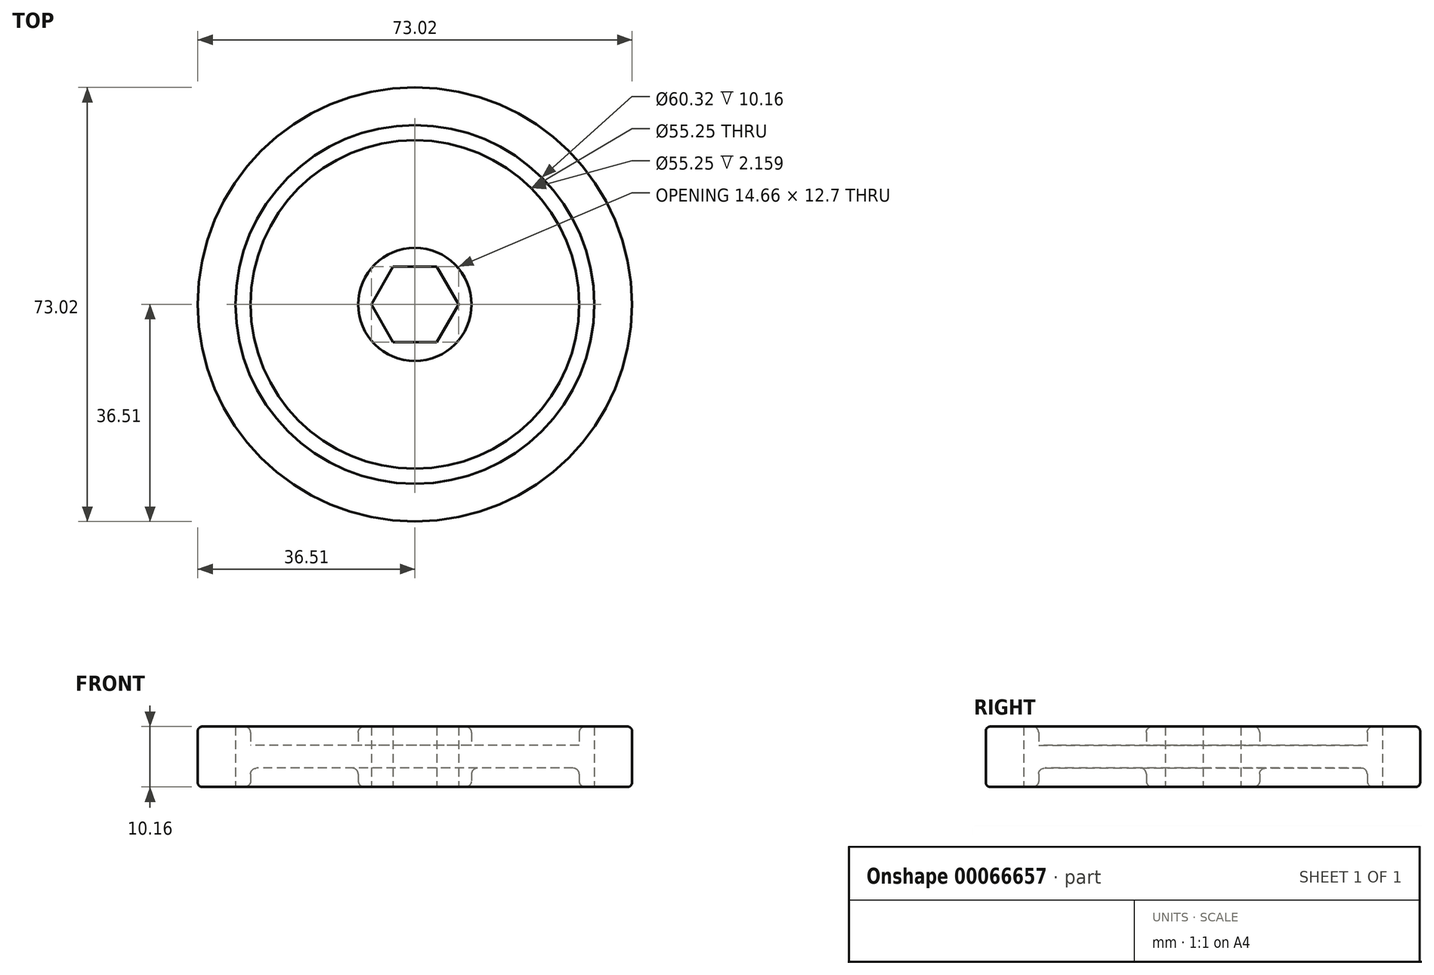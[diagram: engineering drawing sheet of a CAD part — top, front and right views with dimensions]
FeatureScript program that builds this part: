
annotation { "Feature Type Name" : "Feature", "Feature Type Description" : "" }
export const myFeature = defineFeature(function(context is Context, id is Id, definition is map)
    precondition{}
    {
        {
            var Q0;
            Q0=qCreatedBy(makeId("Top.planeOp"),FACE);
            var sketch = newSketch(context, id + "F0", { "sketchPlane" : qUnion([Q0])});
            skCircle(sketch, "E0", {"center": v(0, 0) * mm, "radius": 36.51 * mm});
            skCircle(sketch, "E1", {"center": v(0, 0) * mm, "radius": 27.62 * mm});
            skCircle(sketch, "E2", {"center": v(0, 0) * mm, "radius": 30.16 * mm});
            skCircle(sketch, "E3", {"center": v(0, 0) * mm, "radius": 9.53 * mm});
            skCircle(sketch, "E4.cCircle", {"center": v(0, 0) * mm, "radius": 6.35 * mm, "construction": true});
            skLineSegment(sketch, "E4.0", {"start": v(3.67, -6.35) * mm, "end": v(-3.67, -6.35) * mm});
            skLineSegment(sketch, "E4.1", {"start": v(-3.67, -6.35) * mm, "end": v(-7.33, 0) * mm});
            skLineSegment(sketch, "E4.2", {"start": v(-7.33, 0) * mm, "end": v(-3.67, 6.35) * mm});
            skLineSegment(sketch, "E4.3", {"start": v(-3.67, 6.35) * mm, "end": v(3.67, 6.35) * mm});
            skLineSegment(sketch, "E4.4", {"start": v(3.67, 6.35) * mm, "end": v(7.33, 0) * mm});
            skLineSegment(sketch, "E4.5", {"start": v(7.33, 0) * mm, "end": v(3.67, -6.35) * mm});
            skPoint(sketch, "E4.0.midPoint", {"position": v(0, -6.35) * mm});
            skSolve(sketch);
        }
        {
            var Q0;
            Q0=makeQuery(id+"F0.imprint","IMPRINT",FACE,{"disambiguationData":[TD([[makeQuery(id+"F0.imprint","IMPRINT",EDGE,{"derivedFrom":sQuery(id+"F0.wireOp",EDGE,"E1")}),-1.0]])]});
            var Q1;
            Q1=makeQuery(id+"F0.imprint","IMPRINT",FACE,{"disambiguationData":[TD([[makeQuery(id+"F0.imprint","IMPRINT",EDGE,{"derivedFrom":sQuery(id+"F0.wireOp",EDGE,"E3")}),1.0]])]});
            extrude(context, id + "F1", {"entities" : qUnion([Q0, Q1]), "endBound" : BoundingType.SYMMETRIC, "depth" : 10.16 * mm});
        }
        {
            var Q0;
            Q0=makeQuery(id+"F0.imprint","IMPRINT",FACE,{"disambiguationData":[TD([[makeQuery(id+"F0.imprint","IMPRINT",EDGE,{"derivedFrom":sQuery(id+"F0.wireOp",EDGE,"E1")}),1.0]])]});
            extrude(context, id + "F2", {"entities" : qUnion([Q0]), "operationType" : NewBodyOperationType.ADD, "endBound" : BoundingType.SYMMETRIC, "depth" : 3.8 * mm});
        }
        {
            var Q0;
            Q0=makeQuery(id+"F0.imprint","IMPRINT",FACE,{"disambiguationData":[TD([[makeQuery(id+"F0.imprint","IMPRINT",EDGE,{"derivedFrom":sQuery(id+"F0.wireOp",EDGE,"E0")}),1.0]])]});
            var Q1;
            Q1=makeQuery(id+"F1.opExtrude","CAP_FACE",FACE,{"disambiguationData":[OSD([sQuery(id+"F0.wireOp",EDGE,"E1"),sQuery(id+"F0.wireOp",EDGE,"E2")])],"isStart":false});
            var Q2;
            Q2=makeQuery(id+"F1.opExtrude","CAP_FACE",FACE,{"disambiguationData":[OSD([sQuery(id+"F0.wireOp",EDGE,"E1"),sQuery(id+"F0.wireOp",EDGE,"E2")])],"isStart":true});
            extrude(context, id + "F3", {"entities" : qUnion([Q0]), "endBound" : BoundingType.UP_TO_SURFACE, "endBoundEntityFace" : qUnion([Q1]), "depth" : 25.4 * mm, "hasSecondDirection" : true, "secondDirectionBound" : SecondDirectionBoundingType.UP_TO_SURFACE, "secondDirectionOppositeDirection" : true, "secondDirectionBoundEntityFace" : qUnion([Q2]), "secondDirectionDepth" : 25.4 * mm});
        }
        {
            var Q0;
            Q0=makeQuery(id+"F2.opExtrude","CAP_EDGE",EDGE,{"disambiguationData":[OSD([sQuery(id+"F0.wireOp",EDGE,"E1")])],"isStart":false});
            var Q1;
            Q1=makeQuery(id+"F2.opExtrude","CAP_EDGE",EDGE,{"disambiguationData":[OSD([sQuery(id+"F0.wireOp",EDGE,"E3")])],"isStart":false});
            var Q2;
            Q2=makeQuery(id+"F2.opExtrude","CAP_EDGE",EDGE,{"disambiguationData":[OSD([sQuery(id+"F0.wireOp",EDGE,"E1")])],"isStart":true});
            var Q3;
            Q3=makeQuery(id+"F2.opExtrude","CAP_EDGE",EDGE,{"disambiguationData":[OSD([sQuery(id+"F0.wireOp",EDGE,"E3")])],"isStart":true});
            var Q4;
            Q4=makeQuery(id+"F1.opExtrude","CAP_EDGE",EDGE,{"disambiguationData":[OSD([sQuery(id+"F0.wireOp",EDGE,"E1")])],"isStart":true});
            var Q5;
            Q5=makeQuery(id+"F1.opExtrude","CAP_EDGE",EDGE,{"disambiguationData":[OSD([sQuery(id+"F0.wireOp",EDGE,"E3")])],"isStart":true});
            var Q6;
            Q6=makeQuery(id+"F1.opExtrude","CAP_EDGE",EDGE,{"disambiguationData":[OSD([sQuery(id+"F0.wireOp",EDGE,"E3")])],"isStart":false});
            var Q7;
            Q7=makeQuery(id+"F1.opExtrude","CAP_EDGE",EDGE,{"disambiguationData":[OSD([sQuery(id+"F0.wireOp",EDGE,"E1")])],"isStart":false});
            fillet(context, id + "F4", {"entities" : qUnion([Q0, Q1, Q2, Q3, Q4, Q5, Q6, Q7]), "radius" : 1.02 * mm, "tangentPropagation" : true, "allowEdgeOverflow" : false});
        }
        {
            var Q0;
            Q0=makeQuery(id+"F3.opExtrude","SWEPT_FACE",FACE,{"disambiguationData":[OSD([sQuery(id+"F0.wireOp",EDGE,"E0")])]});
            fillet(context, id + "F5", {"entities" : qUnion([Q0]), "radius" : 0.76 * mm, "tangentPropagation" : true, "allowEdgeOverflow" : false});
        }
    });
